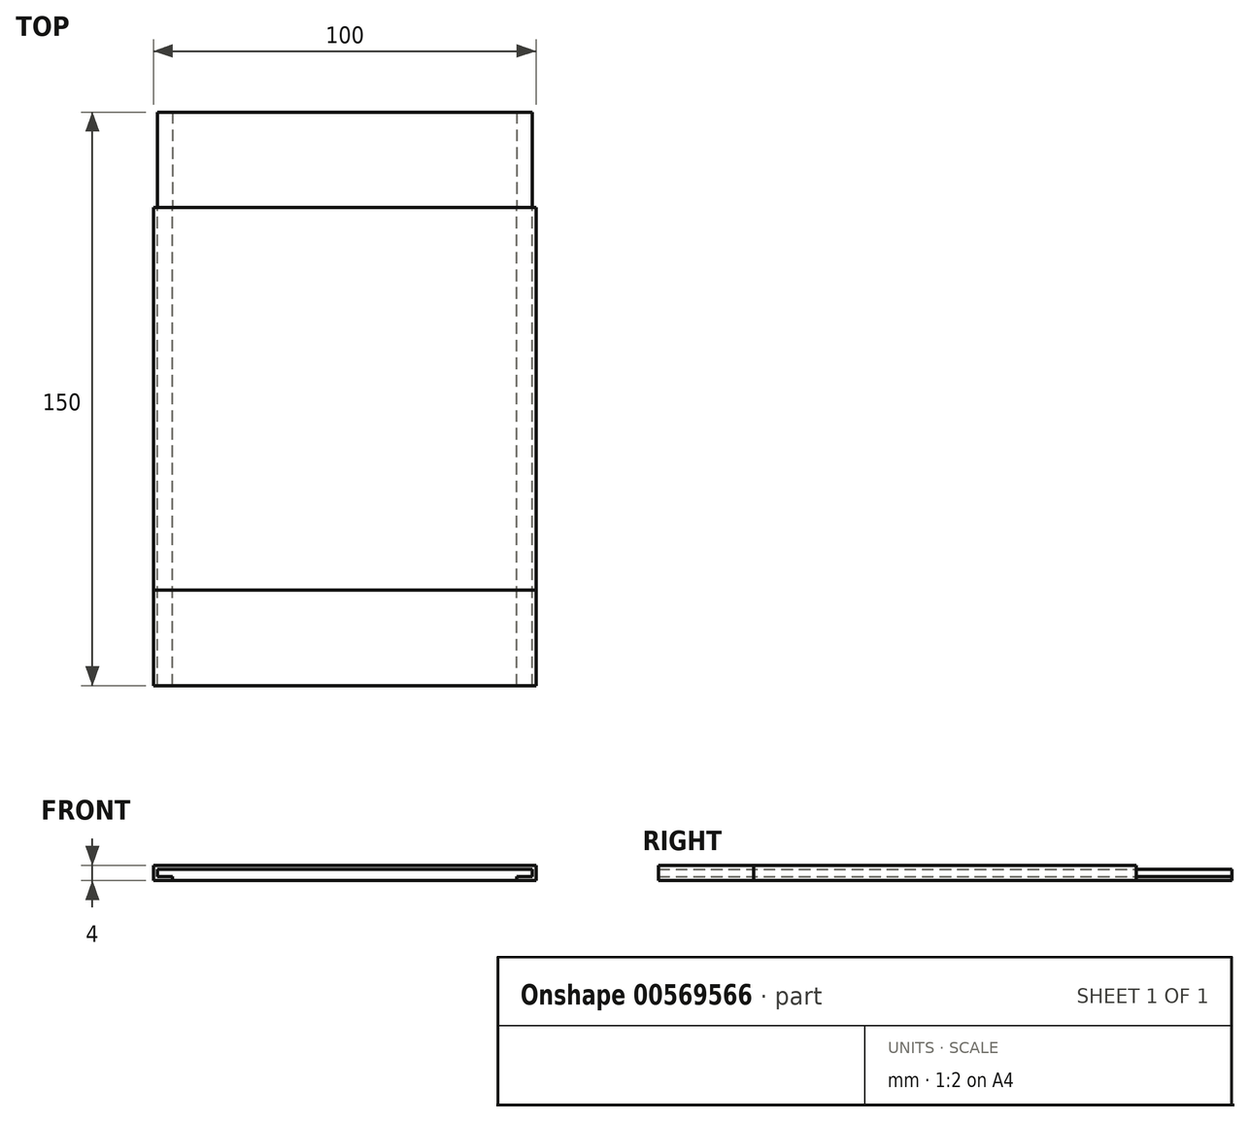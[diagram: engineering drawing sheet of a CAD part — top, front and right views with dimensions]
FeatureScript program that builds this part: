
annotation { "Feature Type Name" : "Feature", "Feature Type Description" : "" }
export const myFeature = defineFeature(function(context is Context, id is Id, definition is map)
    precondition{}
    {
        {
            var Q0;
            Q0=qCreatedBy(makeId("Front.planeOp"),FACE);
            var sketch = newSketch(context, id + "F0", { "sketchPlane" : qUnion([Q0])});
            skLineSegment(sketch, "E0.bottom", {"start": v(50, -2) * mm, "end": v(-50, -2) * mm});
            skLineSegment(sketch, "E0.top", {"start": v(50, 2) * mm, "end": v(-50, 2) * mm});
            skLineSegment(sketch, "E0.left", {"start": v(50, -2) * mm, "end": v(50, 2) * mm});
            skLineSegment(sketch, "E0.right", {"start": v(-50, -2) * mm, "end": v(-50, 2) * mm});
            skPoint(sketch, "E0.middle", {"position": v(0, 0) * mm});
            skLineSegment(sketch, "E1", {"start": v(-49, 1) * mm, "end": v(49, 1) * mm});
            skLineSegment(sketch, "E2", {"start": v(-49, 1) * mm, "end": v(-49, -1.01) * mm});
            skLineSegment(sketch, "E3", {"start": v(49, 1) * mm, "end": v(49, -0.92) * mm});
            skLineSegment(sketch, "E4", {"start": v(-49, -1.01) * mm, "end": v(-45, -1.01) * mm});
            skLineSegment(sketch, "E5", {"start": v(-45, -1.01) * mm, "end": v(-45, -2) * mm});
            skLineSegment(sketch, "E6", {"start": v(49, -0.92) * mm, "end": v(45, -0.92) * mm});
            skLineSegment(sketch, "E7", {"start": v(45, -0.92) * mm, "end": v(45, -2) * mm});
            skPoint(sketch, "E8.orphan", {"position": v(49, -2) * mm});
            skSolve(sketch);
        }
        {
            var Q0;
            Q0=makeQuery(id+"F0.imprint","IMPRINT",FACE,{"disambiguationData":[TD([[makeQuery(id+"F0.imprint","IMPRINT",EDGE,{"derivedFrom":sQuery(id+"F0.wireOp",EDGE,"E1")}),-1.0]])]});
            var Q1;
            Q1=makeQuery(id+"F0.imprint","IMPRINT",FACE,{"disambiguationData":[TD([[makeQuery(id+"F0.imprint","IMPRINT",EDGE,{"derivedFrom":sQuery(id+"F0.wireOp",EDGE,"E0.top")}),1.0]])]});
            extrude(context, id + "F1", {"entities" : qUnion([Q0, Q1]), "depth" : 100 * mm, "offsetDistance" : 25 * mm});
        }
        {
            var Q0;
            Q0=makeQuery(id+"F0.imprint","IMPRINT",FACE,{"disambiguationData":[TD([[makeQuery(id+"F0.imprint","IMPRINT",EDGE,{"derivedFrom":sQuery(id+"F0.wireOp",EDGE,"E1")}),-1.0]])]});
            extrude(context, id + "F2", {"entities" : qUnion([Q0]), "operationType" : NewBodyOperationType.ADD, "oppositeDirection" : true, "depth" : 25 * mm, "offsetDistance" : 25 * mm});
        }
        {
            var Q0;
            Q0=makeQuery(id+"F0.imprint","IMPRINT",FACE,{"disambiguationData":[TD([[makeQuery(id+"F0.imprint","IMPRINT",EDGE,{"derivedFrom":sQuery(id+"F0.wireOp",EDGE,"E0.top")}),1.0]])]});
            extrude(context, id + "F3", {"entities" : qUnion([Q0]), "depth" : 125 * mm, "offsetDistance" : 25 * mm});
        }
    });
